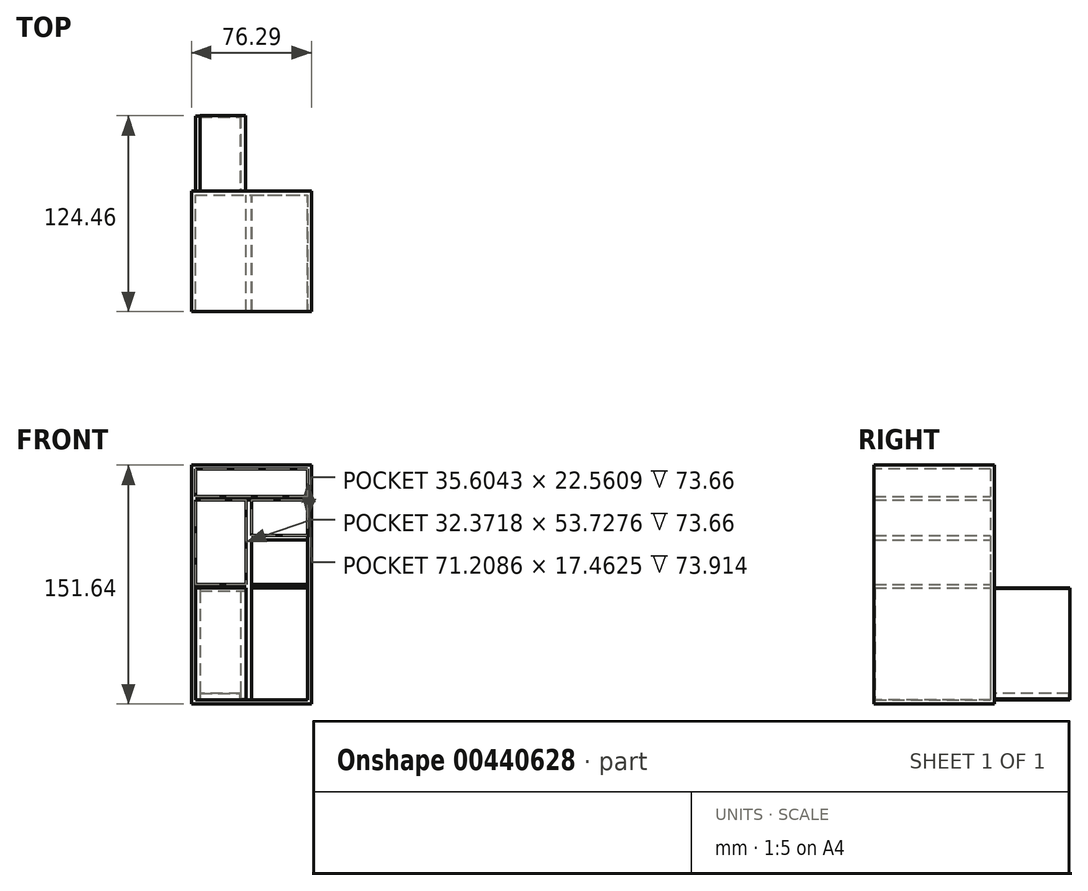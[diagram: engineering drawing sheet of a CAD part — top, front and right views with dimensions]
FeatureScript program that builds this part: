
annotation { "Feature Type Name" : "Feature", "Feature Type Description" : "" }
export const myFeature = defineFeature(function(context is Context, id is Id, definition is map)
    precondition{}
    {
        {
            var Q0;
            Q0=qCreatedBy(makeId("Front.planeOp"),FACE);
            var sketch = newSketch(context, id + "F0", { "sketchPlane" : qUnion([Q0])});
            skLineSegment(sketch, "E0.bottom", {"start": v(-76.29, 75.82) * mm, "end": v(0, 75.82) * mm});
            skLineSegment(sketch, "E0.top", {"start": v(-76.29, -75.82) * mm, "end": v(0, -75.82) * mm});
            skLineSegment(sketch, "E0.left", {"start": v(-76.29, 75.82) * mm, "end": v(-76.29, -75.82) * mm});
            skLineSegment(sketch, "E0.right", {"start": v(0, 75.82) * mm, "end": v(0, -75.82) * mm});
            skSolve(sketch);
        }
        {
            var Q0;
            Q0=makeQuery(id+"F0.imprint","IMPRINT",FACE,{"disambiguationData":[TD([[makeQuery(id+"F0.imprint","IMPRINT",EDGE,{"derivedFrom":sQuery(id+"F0.wireOp",EDGE,"E0.bottom")}),-1.0]])]});
            extrude(context, id + "F1", {"entities" : qUnion([Q0]), "oppositeDirection" : true, "depth" : 76.45 * mm});
        }
        {
            var Q0;
            Q0=makeQuery(id+"F1.opExtrude","CAP_FACE",FACE,{"disambiguationData":[OSD([sQuery(id+"F0.wireOp",EDGE,"E0.bottom"),sQuery(id+"F0.wireOp",EDGE,"E0.top"),sQuery(id+"F0.wireOp",EDGE,"E0.left"),sQuery(id+"F0.wireOp",EDGE,"E0.right")])],"isStart":true});
            shell(context, id + "F2", {"entities" : qUnion([Q0]), "thickness" : 2.54 * mm});
        }
        {
            var Q0;
            Q0=makeQuery(id+"F2.opShell","OFFSET_FACE",FACE,{"disambiguationData":[OSD([sQuery(id+"F0.wireOp",EDGE,"E0.bottom"),sQuery(id+"F0.wireOp",EDGE,"E0.top"),sQuery(id+"F0.wireOp",EDGE,"E0.left"),sQuery(id+"F0.wireOp",EDGE,"E0.right")])]});
            var sketch = newSketch(context, id + "F3", { "sketchPlane" : qUnion([Q0])});
            skLineSegment(sketch, "E1.bottom", {"start": v(-73.75, 55.82) * mm, "end": v(-2.54, 55.82) * mm});
            skLineSegment(sketch, "E1.top", {"start": v(-73.75, 53.73) * mm, "end": v(-2.54, 53.73) * mm});
            skLineSegment(sketch, "E1.left", {"start": v(-73.75, 55.82) * mm, "end": v(-73.75, 53.73) * mm});
            skLineSegment(sketch, "E1.right", {"start": v(-2.54, 55.82) * mm, "end": v(-2.54, 53.73) * mm});
            skSolve(sketch);
        }
        {
            var Q0;
            Q0 = qSketchRegion(id + "F3", true);
            extrude(context, id + "F4", {"entities" : qUnion([Q0]), "operationType" : NewBodyOperationType.ADD, "depth" : 73.9 * mm});
        }
        {
            var Q0;
            {var subQ0=sQuery(id+"F0.wireOp",EDGE,"E0.top");var subQ1=sQuery(id+"F0.wireOp",EDGE,"E0.left");var subQ2=sQuery(id+"F0.wireOp",EDGE,"E0.right");Q0=makeQuery(id+"F4.boolean.opBoolean","SPLIT",FACE,{"disambiguationData":[TD([makeQuery(id+"F2.opShell","OFFSET_FACE",FACE,{"disambiguationData":[OSD([subQ0])]})])],"derivedFrom":makeQuery(id+"F2.opShell","OFFSET_FACE",FACE,{"disambiguationData":[OSD([sQuery(id+"F0.wireOp",EDGE,"E0.bottom"),subQ0,subQ1,subQ2])]})});}
            var sketch = newSketch(context, id + "F5", { "sketchPlane" : qUnion([Q0])});
            skLineSegment(sketch, "E2.bottom", {"start": v(-41.38, 53.73) * mm, "end": v(-38.14, 53.73) * mm});
            skLineSegment(sketch, "E2.top", {"start": v(-41.38, -73.28) * mm, "end": v(-38.14, -73.28) * mm});
            skLineSegment(sketch, "E2.left", {"start": v(-41.38, 53.73) * mm, "end": v(-41.38, -73.28) * mm});
            skLineSegment(sketch, "E2.right", {"start": v(-38.14, 53.73) * mm, "end": v(-38.14, -73.28) * mm});
            skSolve(sketch);
        }
        {
            var Q0;
            Q0=makeQuery(id+"F5.imprint","IMPRINT",FACE,{"disambiguationData":[TD([[makeQuery(id+"F5.imprint","IMPRINT",EDGE,{"derivedFrom":sQuery(id+"F5.wireOp",EDGE,"E2.bottom")}),-1.0]])]});
            extrude(context, id + "F6", {"entities" : qUnion([Q0]), "operationType" : NewBodyOperationType.ADD, "depth" : 73.66 * mm});
        }
        {
            var Q0;
            {var subQ0=sQuery(id+"F0.wireOp",EDGE,"E0.top");var subQ1=makeQuery(id+"F2.opShell","OFFSET_FACE",FACE,{"disambiguationData":[OSD([subQ0])]});var subQ2=sQuery(id+"F0.wireOp",EDGE,"E0.left");var subQ3=makeQuery(id+"F2.opShell","OFFSET_FACE",FACE,{"disambiguationData":[OSD([subQ2])]});var subQ5=sQuery(id+"F0.wireOp",EDGE,"E0.right");Q0=makeQuery(id+"F6.boolean.opBoolean","SPLIT",FACE,{"disambiguationData":[TD([subQ3])],"derivedFrom":makeQuery(id+"F4.boolean.opBoolean","SPLIT",FACE,{"disambiguationData":[TD([subQ1])],"derivedFrom":makeQuery(id+"F2.opShell","OFFSET_FACE",FACE,{"disambiguationData":[OSD([sQuery(id+"F0.wireOp",EDGE,"E0.bottom"),subQ0,subQ2,subQ5])]})})});}
            var sketch = newSketch(context, id + "F7", { "sketchPlane" : qUnion([Q0])});
            skLineSegment(sketch, "E3.bottom", {"start": v(-73.75, 0) * mm, "end": v(-41.38, 0) * mm});
            skLineSegment(sketch, "E3.top", {"start": v(-73.75, -2.1) * mm, "end": v(-41.38, -2.1) * mm});
            skLineSegment(sketch, "E3.left", {"start": v(-73.75, 0) * mm, "end": v(-73.75, -2.1) * mm});
            skLineSegment(sketch, "E3.right", {"start": v(-41.38, 0) * mm, "end": v(-41.38, -2.1) * mm});
            skSolve(sketch);
        }
        {
            var Q0;
            Q0 = qSketchRegion(id + "F7", true);
            extrude(context, id + "F8", {"entities" : qUnion([Q0]), "operationType" : NewBodyOperationType.ADD, "depth" : 73.66 * mm});
        }
        {
            var Q0;
            {var subQ0=sQuery(id+"F0.wireOp",EDGE,"E0.top");var subQ1=makeQuery(id+"F2.opShell","OFFSET_FACE",FACE,{"disambiguationData":[OSD([subQ0])]});var subQ2=sQuery(id+"F0.wireOp",EDGE,"E0.right");var subQ3=makeQuery(id+"F2.opShell","OFFSET_FACE",FACE,{"disambiguationData":[OSD([subQ2])]});var subQ5=sQuery(id+"F0.wireOp",EDGE,"E0.left");Q0=makeQuery(id+"F6.boolean.opBoolean","SPLIT",FACE,{"disambiguationData":[TD([subQ3])],"derivedFrom":makeQuery(id+"F4.boolean.opBoolean","SPLIT",FACE,{"disambiguationData":[TD([subQ1])],"derivedFrom":makeQuery(id+"F2.opShell","OFFSET_FACE",FACE,{"disambiguationData":[OSD([sQuery(id+"F0.wireOp",EDGE,"E0.bottom"),subQ0,subQ5,subQ2])]})})});}
            var sketch = newSketch(context, id + "F9", { "sketchPlane" : qUnion([Q0])});
            skLineSegment(sketch, "E4.bottom", {"start": v(-38.14, 31.17) * mm, "end": v(-2.54, 31.17) * mm});
            skLineSegment(sketch, "E4.top", {"start": v(-38.14, 28.38) * mm, "end": v(-2.54, 28.38) * mm});
            skLineSegment(sketch, "E4.left", {"start": v(-38.14, 31.17) * mm, "end": v(-38.14, 28.38) * mm});
            skLineSegment(sketch, "E4.right", {"start": v(-2.54, 31.17) * mm, "end": v(-2.54, 28.38) * mm});
            skSolve(sketch);
        }
        {
            var Q0;
            {var subQ0=sQuery(id+"F9.wireOp",EDGE,"E4.top");Q0=makeQuery(id+"F9.imprint","IMPRINT",FACE,{"disambiguationData":[TD([[makeQuery(id+"F9.imprint","IMPRINT",EDGE,{"derivedFrom":subQ0}),-1.0]])]});}
            var sketch = newSketch(context, id + "F10", { "sketchPlane" : qUnion([Q0])});
            skLineSegment(sketch, "E5.bottom", {"start": v(-37.72, 0) * mm, "end": v(-2.37, 0) * mm});
            skLineSegment(sketch, "E5.top", {"start": v(-37.72, -2.1) * mm, "end": v(-2.37, -2.1) * mm});
            skLineSegment(sketch, "E5.left", {"start": v(-37.72, 0) * mm, "end": v(-37.72, -2.1) * mm});
            skLineSegment(sketch, "E5.right", {"start": v(-2.37, 0) * mm, "end": v(-2.37, -2.1) * mm});
            skSolve(sketch);
        }
        {
            var Q0;
            Q0 = qSketchRegion(id + "F10", true);
            extrude(context, id + "F11", {"entities" : qUnion([Q0]), "operationType" : NewBodyOperationType.ADD, "depth" : 73.66 * mm});
        }
        {
            var Q0;
            Q0 = qSketchRegion(id + "F9", true);
            extrude(context, id + "F12", {"entities" : qUnion([Q0]), "operationType" : NewBodyOperationType.ADD, "depth" : 73.66 * mm});
        }
        {
            var Q0;
            {var subQ0=sQuery(id+"F0.wireOp",EDGE,"E0.top");var subQ1=makeQuery(id+"F2.opShell","OFFSET_FACE",FACE,{"disambiguationData":[OSD([subQ0])]});var subQ2=sQuery(id+"F0.wireOp",EDGE,"E0.left");var subQ3=makeQuery(id+"F2.opShell","OFFSET_FACE",FACE,{"disambiguationData":[OSD([subQ2])]});var subQ6=sQuery(id+"F0.wireOp",EDGE,"E0.right");Q0=makeQuery(id+"F8.boolean.opBoolean","SPLIT",FACE,{"disambiguationData":[TD([subQ1])],"derivedFrom":makeQuery(id+"F6.boolean.opBoolean","SPLIT",FACE,{"disambiguationData":[TD([subQ3])],"derivedFrom":makeQuery(id+"F4.boolean.opBoolean","SPLIT",FACE,{"disambiguationData":[TD([subQ1])],"derivedFrom":makeQuery(id+"F2.opShell","OFFSET_FACE",FACE,{"disambiguationData":[OSD([sQuery(id+"F0.wireOp",EDGE,"E0.bottom"),subQ0,subQ2,subQ6])]})})})});}
            var sketch = newSketch(context, id + "F13", { "sketchPlane" : qUnion([Q0])});
            skLineSegment(sketch, "E6.bottom", {"start": v(-73.75, -2.1) * mm, "end": v(-70.75, -2.1) * mm});
            skLineSegment(sketch, "E6.top", {"start": v(-73.75, -73.28) * mm, "end": v(-70.75, -73.28) * mm});
            skLineSegment(sketch, "E6.left", {"start": v(-73.75, -2.1) * mm, "end": v(-73.75, -73.28) * mm});
            skLineSegment(sketch, "E6.right", {"start": v(-70.75, -2.1) * mm, "end": v(-70.75, -73.28) * mm});
            skSolve(sketch);
        }
        {
            var Q0;
            {var subQ0=sQuery(id+"F13.wireOp",EDGE,"E6.right");Q0=makeQuery(id+"F13.imprint","IMPRINT",FACE,{"disambiguationData":[TD([[makeQuery(id+"F13.imprint","IMPRINT",EDGE,{"derivedFrom":subQ0}),1.0]])]});}
            var sketch = newSketch(context, id + "F14", { "sketchPlane" : qUnion([Q0])});
            skLineSegment(sketch, "E7.bottom", {"start": v(-70.75, -2.56) * mm, "end": v(-41.91, -2.56) * mm});
            skLineSegment(sketch, "E7.top", {"start": v(-70.75, -4.19) * mm, "end": v(-41.91, -4.19) * mm});
            skLineSegment(sketch, "E7.left", {"start": v(-70.75, -2.56) * mm, "end": v(-70.75, -4.19) * mm});
            skLineSegment(sketch, "E7.right", {"start": v(-41.91, -2.56) * mm, "end": v(-41.91, -4.19) * mm});
            skSolve(sketch);
        }
        {
            var Q0;
            {var subQ0=sQuery(id+"F13.wireOp",EDGE,"E6.right");Q0=makeQuery(id+"F13.imprint","IMPRINT",FACE,{"disambiguationData":[TD([[makeQuery(id+"F13.imprint","IMPRINT",EDGE,{"derivedFrom":subQ0}),1.0]])]});}
            var sketch = newSketch(context, id + "F15", { "sketchPlane" : qUnion([Q0])});
            skLineSegment(sketch, "E8.bottom", {"start": v(-41.91, -3.95) * mm, "end": v(-44.93, -3.95) * mm});
            skLineSegment(sketch, "E8.top", {"start": v(-41.91, -72.8) * mm, "end": v(-44.93, -72.8) * mm});
            skLineSegment(sketch, "E8.left", {"start": v(-41.91, -3.95) * mm, "end": v(-41.91, -72.8) * mm});
            skLineSegment(sketch, "E8.right", {"start": v(-44.93, -3.95) * mm, "end": v(-44.93, -72.8) * mm});
            skSolve(sketch);
        }
        {
            var Q0;
            {var subQ0=sQuery(id+"F13.wireOp",EDGE,"E6.right");Q0=makeQuery(id+"F13.imprint","IMPRINT",FACE,{"disambiguationData":[TD([[makeQuery(id+"F13.imprint","IMPRINT",EDGE,{"derivedFrom":subQ0}),1.0]])]});}
            var sketch = newSketch(context, id + "F16", { "sketchPlane" : qUnion([Q0])});
            skLineSegment(sketch, "E9.bottom", {"start": v(-70.75, -73.03) * mm, "end": v(-45.4, -73.03) * mm});
            skLineSegment(sketch, "E9.top", {"start": v(-70.75, -69.31) * mm, "end": v(-45.4, -69.31) * mm});
            skLineSegment(sketch, "E9.left", {"start": v(-70.75, -73.03) * mm, "end": v(-70.75, -69.31) * mm});
            skLineSegment(sketch, "E9.right", {"start": v(-45.4, -73.03) * mm, "end": v(-45.4, -69.31) * mm});
            skSolve(sketch);
        }
        {
            var Q0;
            Q0 = qSketchRegion(id + "F16", true);
            extrude(context, id + "F17", {"entities" : qUnion([Q0]), "operationType" : NewBodyOperationType.ADD, "oppositeDirection" : true, "depth" : 49.78 * mm});
        }
        {
            var Q0;
            Q0 = qSketchRegion(id + "F15", true);
            extrude(context, id + "F18", {"entities" : qUnion([Q0]), "operationType" : NewBodyOperationType.ADD, "oppositeDirection" : true, "depth" : 50.3 * mm});
        }
        {
            var Q0;
            Q0 = qSketchRegion(id + "F14", true);
            extrude(context, id + "F19", {"entities" : qUnion([Q0]), "operationType" : NewBodyOperationType.ADD, "oppositeDirection" : true, "depth" : 50.55 * mm});
        }
        {
            var Q0;
            Q0 = qSketchRegion(id + "F13", true);
            extrude(context, id + "F20", {"entities" : qUnion([Q0]), "operationType" : NewBodyOperationType.ADD, "oppositeDirection" : true, "depth" : 50.3 * mm});
        }
        {
            var Q0;
            Q0=makeQuery(id+"F1.opExtrude","CAP_FACE",FACE,{"disambiguationData":[OSD([sQuery(id+"F0.wireOp",EDGE,"E0.bottom"),sQuery(id+"F0.wireOp",EDGE,"E0.top"),sQuery(id+"F0.wireOp",EDGE,"E0.left"),sQuery(id+"F0.wireOp",EDGE,"E0.right")])],"isStart":false});
            var sketch = newSketch(context, id + "F21", { "sketchPlane" : qUnion([Q0])});
            skLineSegment(sketch, "E10.bottom", {"start": v(44.93, -4.19) * mm, "end": v(70.75, -4.19) * mm});
            skLineSegment(sketch, "E10.top", {"start": v(44.93, -69.31) * mm, "end": v(70.75, -69.31) * mm});
            skLineSegment(sketch, "E10.left", {"start": v(44.93, -4.19) * mm, "end": v(44.93, -69.31) * mm});
            skLineSegment(sketch, "E10.right", {"start": v(70.75, -4.19) * mm, "end": v(70.75, -69.31) * mm});
            skSolve(sketch);
        }
        {
            var Q0;
            Q0=makeQuery(id+"F21.imprint","IMPRINT",FACE,{"disambiguationData":[TD([[makeQuery(id+"F21.imprint","IMPRINT",EDGE,{"derivedFrom":sQuery(id+"F21.wireOp",EDGE,"E10.bottom")}),1.0]])]});
            extrude(context, id + "F22", {"entities" : qUnion([Q0]), "operationType" : NewBodyOperationType.ADD, "depth" : 47.5 * mm});
        }
        {
            var Q0;
            {var subQ0=sQuery(id+"F0.wireOp",EDGE,"E0.top");var subQ1=makeQuery(id+"F2.opShell","OFFSET_FACE",FACE,{"disambiguationData":[OSD([subQ0])]});var subQ2=sQuery(id+"F0.wireOp",EDGE,"E0.left");var subQ3=makeQuery(id+"F2.opShell","OFFSET_FACE",FACE,{"disambiguationData":[OSD([subQ2])]});var subQ6=sQuery(id+"F0.wireOp",EDGE,"E0.right");Q0=makeQuery(id+"F8.boolean.opBoolean","SPLIT",FACE,{"disambiguationData":[TD([subQ1])],"derivedFrom":makeQuery(id+"F6.boolean.opBoolean","SPLIT",FACE,{"disambiguationData":[TD([subQ3])],"derivedFrom":makeQuery(id+"F4.boolean.opBoolean","SPLIT",FACE,{"disambiguationData":[TD([subQ1])],"derivedFrom":makeQuery(id+"F2.opShell","OFFSET_FACE",FACE,{"disambiguationData":[OSD([sQuery(id+"F0.wireOp",EDGE,"E0.bottom"),subQ0,subQ2,subQ6])]})})})});}
            extrude(context, id + "F23", {"entities" : qUnion([Q0]), "operationType" : NewBodyOperationType.ADD, "depth" : 73.4 * mm});
        }
    });
